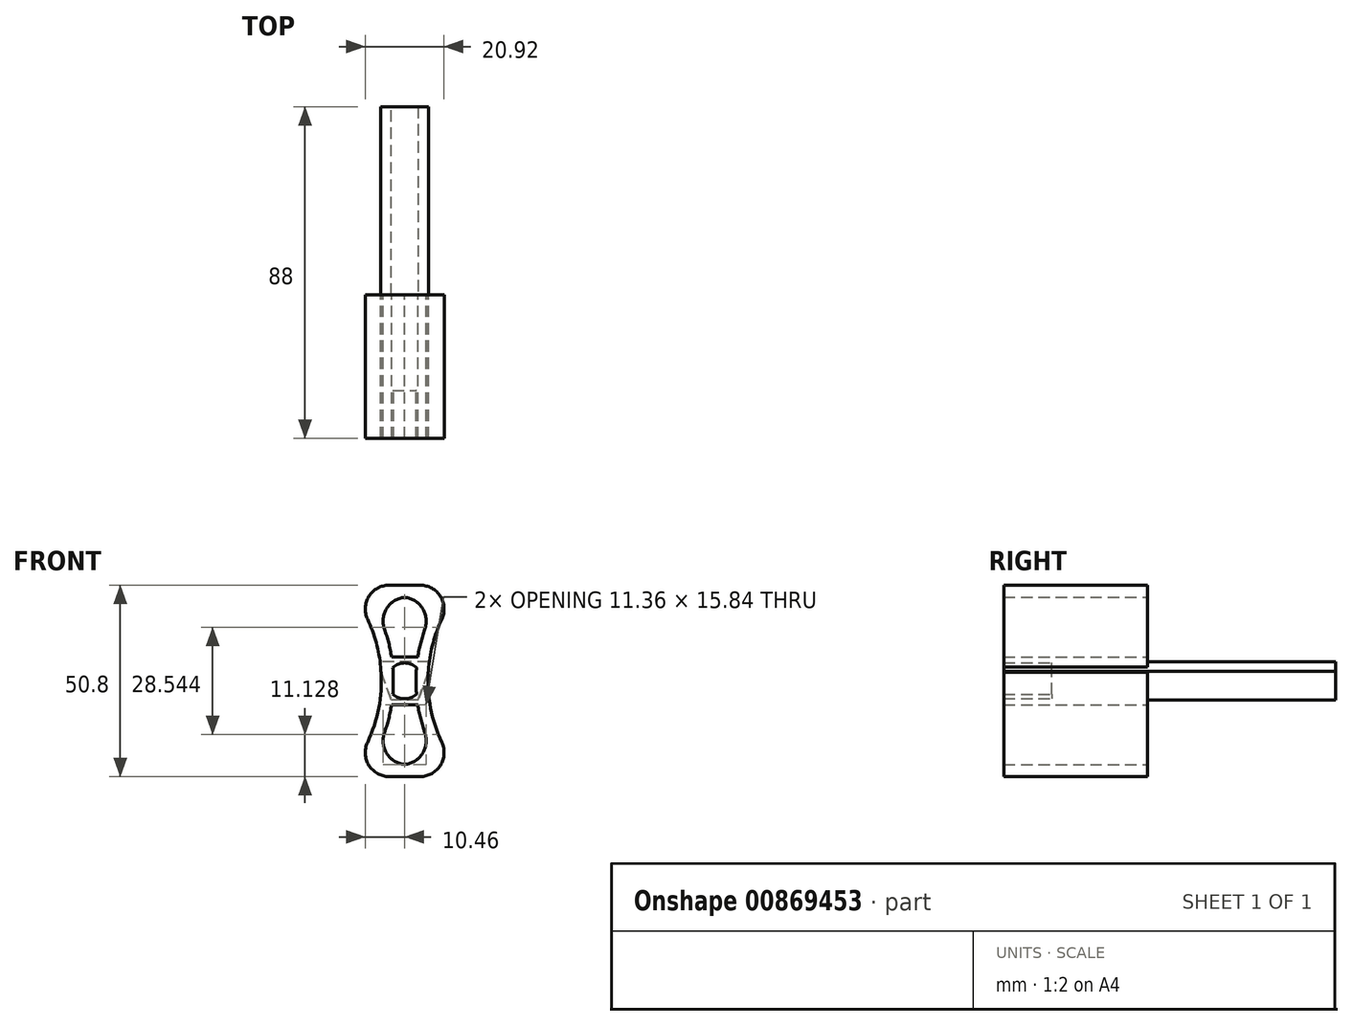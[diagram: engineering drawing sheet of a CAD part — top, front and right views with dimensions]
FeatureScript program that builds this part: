
annotation { "Feature Type Name" : "Feature", "Feature Type Description" : "" }
export const myFeature = defineFeature(function(context is Context, id is Id, definition is map)
    precondition{}
    {
        {
            var Q0;
            Q0=qCreatedBy(makeId("Front.planeOp"),FACE);
            var sketch = newSketch(context, id + "F0", { "sketchPlane" : qUnion([Q0])});
            skLineSegment(sketch, "E0.bottom", {"start": v(-15.87, 25.4) * mm, "end": v(15.88, 25.4) * mm});
            skLineSegment(sketch, "E0.top", {"start": v(-15.88, -25.4) * mm, "end": v(15.87, -25.4) * mm});
            skPoint(sketch, "E0.middle", {"position": v(0, 0) * mm});
            skArc(sketch, "E1", {"start": v(-15.88, -25.4) * mm, "mid": v(-6.17, 0) * mm, "end": v(-15.88, 25.4) * mm});
            skArc(sketch, "E2.MirrorCS", {"start": v(15.88, -25.4) * mm, "mid": v(6.17, 0) * mm, "end": v(15.88, 25.4) * mm});
            skLineSegment(sketch, "E3.0", {"start": v(-9.5, 22.23) * mm, "end": v(9.5, 22.23) * mm});
            skArc(sketch, "E3.1", {"start": v(-9.5, -22.22) * mm, "mid": v(-3, 0) * mm, "end": v(-9.5, 22.22) * mm});
            skLineSegment(sketch, "E3.2", {"start": v(-9.5, -22.23) * mm, "end": v(9.5, -22.23) * mm});
            skArc(sketch, "E3.3", {"start": v(9.5, -22.22) * mm, "mid": v(3, 0) * mm, "end": v(9.5, 22.22) * mm});
            skSolve(sketch);
        }
        {
            var Q0;
            Q0=makeQuery(id+"F0.imprint","IMPRINT",FACE,{"disambiguationData":[TD([[makeQuery(id+"F0.imprint","IMPRINT",EDGE,{"derivedFrom":sQuery(id+"F0.wireOp",EDGE,"E0.bottom")}),-1.0]])]});
            extrude(context, id + "F1", {"entities" : qUnion([Q0]), "depth" : 25.4 * mm, "offsetDistance" : 25.4 * mm, "hasSecondDirection" : true, "secondDirectionOppositeDirection" : true, "secondDirectionDepth" : 12.7 * mm});
        }
        {
            var Q0;
            Q0=makeQuery(id+"F1.opExtrude","SWEPT_EDGE",EDGE,{"disambiguationData":[OSD([sQuery(id+"F0.wireOp",EDGE,"E0.bottom"),sQuery(id+"F0.wireOp",EDGE,"E1")])]});
            var Q1;
            Q1=makeQuery(id+"F1.opExtrude","SWEPT_EDGE",EDGE,{"disambiguationData":[OSD([sQuery(id+"F0.wireOp",EDGE,"E0.top"),sQuery(id+"F0.wireOp",EDGE,"E1")])]});
            var Q2;
            Q2=makeQuery(id+"F1.opExtrude","SWEPT_EDGE",EDGE,{"disambiguationData":[OSD([sQuery(id+"F0.wireOp",EDGE,"E0.bottom"),sQuery(id+"F0.wireOp",EDGE,"E2.MirrorCS")])]});
            var Q3;
            Q3=makeQuery(id+"F1.opExtrude","SWEPT_EDGE",EDGE,{"disambiguationData":[OSD([sQuery(id+"F0.wireOp",EDGE,"E0.top"),sQuery(id+"F0.wireOp",EDGE,"E2.MirrorCS")])]});
            var Q4;
            Q4=makeQuery(id+"F1.opExtrude","SWEPT_EDGE",EDGE,{"disambiguationData":[OSD([sQuery(id+"F0.wireOp",EDGE,"E3.0"),sQuery(id+"F0.wireOp",EDGE,"E3.3")])]});
            var Q5;
            Q5=makeQuery(id+"F1.opExtrude","SWEPT_EDGE",EDGE,{"disambiguationData":[OSD([sQuery(id+"F0.wireOp",EDGE,"E3.2"),sQuery(id+"F0.wireOp",EDGE,"E3.3")])]});
            var Q6;
            Q6=makeQuery(id+"F1.opExtrude","SWEPT_EDGE",EDGE,{"disambiguationData":[OSD([sQuery(id+"F0.wireOp",EDGE,"E3.0"),sQuery(id+"F0.wireOp",EDGE,"E3.1")])]});
            var Q7;
            Q7=makeQuery(id+"F1.opExtrude","SWEPT_EDGE",EDGE,{"disambiguationData":[OSD([sQuery(id+"F0.wireOp",EDGE,"E3.1"),sQuery(id+"F0.wireOp",EDGE,"E3.2")])]});
            fillet(context, id + "F2", {"entities" : qUnion([Q0, Q1, Q2, Q3, Q4, Q5, Q6, Q7]), "radius" : 6.35 * mm, "tangentPropagation" : true, "allowEdgeOverflow" : false});
        }
        {
            var Q0;
            Q0=qCreatedBy(makeId("Front.planeOp"),FACE);
            var sketch = newSketch(context, id + "F3", { "sketchPlane" : qUnion([Q0])});
            skLineSegment(sketch, "E4.bottom", {"start": v(6.35, 6.35) * mm, "end": v(-6.35, 6.35) * mm});
            skLineSegment(sketch, "E4.top", {"start": v(6.35, -6.35) * mm, "end": v(-6.35, -6.35) * mm});
            skLineSegment(sketch, "E4.left", {"start": v(6.35, 6.35) * mm, "end": v(6.35, -6.35) * mm});
            skLineSegment(sketch, "E4.right", {"start": v(-6.35, 6.35) * mm, "end": v(-6.35, -6.35) * mm});
            skPoint(sketch, "E4.middle", {"position": v(0, 0) * mm});
            skCircle(sketch, "E5", {"center": v(0, 0) * mm, "radius": 4.76 * mm});
            skSolve(sketch);
        }
        {
            var Q0;
            Q0=makeQuery(id+"F3.imprint","IMPRINT",FACE,{"disambiguationData":[TD([[makeQuery(id+"F3.imprint","IMPRINT",EDGE,{"derivedFrom":sQuery(id+"F3.wireOp",EDGE,"E4.bottom")}),1.0]])]});
            extrude(context, id + "F4", {"entities" : qUnion([Q0]), "operationType" : NewBodyOperationType.ADD, "depth" : 25.4 * mm, "offsetDistance" : 25.4 * mm});
        }
        {
            var Q0;
            Q0=qCreatedBy(makeId("Front.planeOp"),FACE);
            var sketch = newSketch(context, id + "F5", { "sketchPlane" : qUnion([Q0])});
            skLineSegment(sketch, "E6.bottom", {"start": v(-6.35, 6.35) * mm, "end": v(6.35, 6.35) * mm});
            skLineSegment(sketch, "E6.top", {"start": v(-6.35, -6.35) * mm, "end": v(6.35, -6.35) * mm});
            skLineSegment(sketch, "E6.left", {"start": v(-6.35, 6.35) * mm, "end": v(-6.35, -6.35) * mm});
            skLineSegment(sketch, "E6.right", {"start": v(6.35, 6.35) * mm, "end": v(6.35, -6.35) * mm});
            skPoint(sketch, "E6.middle", {"position": v(0, 0) * mm});
            skSolve(sketch);
        }
        {
            var Q0;
            Q0 = qSketchRegion(id + "F5", true);
            extrude(context, id + "F6", {"entities" : qUnion([Q0]), "operationType" : NewBodyOperationType.ADD, "oppositeDirection" : true, "depth" : 12.7 * mm, "offsetDistance" : 25.4 * mm, "hasSecondDirection" : true, "secondDirectionOppositeDirection" : false, "secondDirectionDepth" : 12.7 * mm});
        }
        {
            var Q0;
            Q0=qCreatedBy(makeId("Right.planeOp"),FACE);
            var sketch = newSketch(context, id + "F7", { "sketchPlane" : qUnion([Q0])});
            skLineSegment(sketch, "E7.bottom", {"start": v(-0.9, 5.04) * mm, "end": v(62.6, 5.04) * mm});
            skLineSegment(sketch, "E7.top", {"start": v(-0.9, -5.04) * mm, "end": v(62.6, -5.04) * mm});
            skLineSegment(sketch, "E7.left", {"start": v(-0.9, 5.04) * mm, "end": v(-0.9, -5.04) * mm});
            skLineSegment(sketch, "E7.right", {"start": v(62.6, 5.04) * mm, "end": v(62.6, -5.04) * mm});
            skSolve(sketch);
        }
        {
            var Q0;
            Q0 = qSketchRegion(id + "F7", true);
            extrude(context, id + "F8", {"entities" : qUnion([Q0]), "operationType" : NewBodyOperationType.ADD, "endBound" : BoundingType.SYMMETRIC, "depth" : 12.7 * mm, "offsetDistance" : 25.4 * mm});
        }
        {
            var Q0;
            Q0=makeQuery(id+"F8.opExtrude","CAP_EDGE",EDGE,{"disambiguationData":[OSD([sQuery(id+"F7.wireOp",EDGE,"E7.top")])],"isStart":false});
            var Q1;
            Q1=makeQuery(id+"F8.opExtrude","CAP_EDGE",EDGE,{"disambiguationData":[OSD([sQuery(id+"F7.wireOp",EDGE,"E7.top")])],"isStart":true});
            chamfer(context, id + "F9", {"entities" : qUnion([Q0, Q1]), "chamferType" : ChamferType.OFFSET_ANGLE, "width" : 7.62 * mm, "oppositeDirection" : false, "angle" : 20 * degree, "tangentPropagation" : true});
        }
    });
